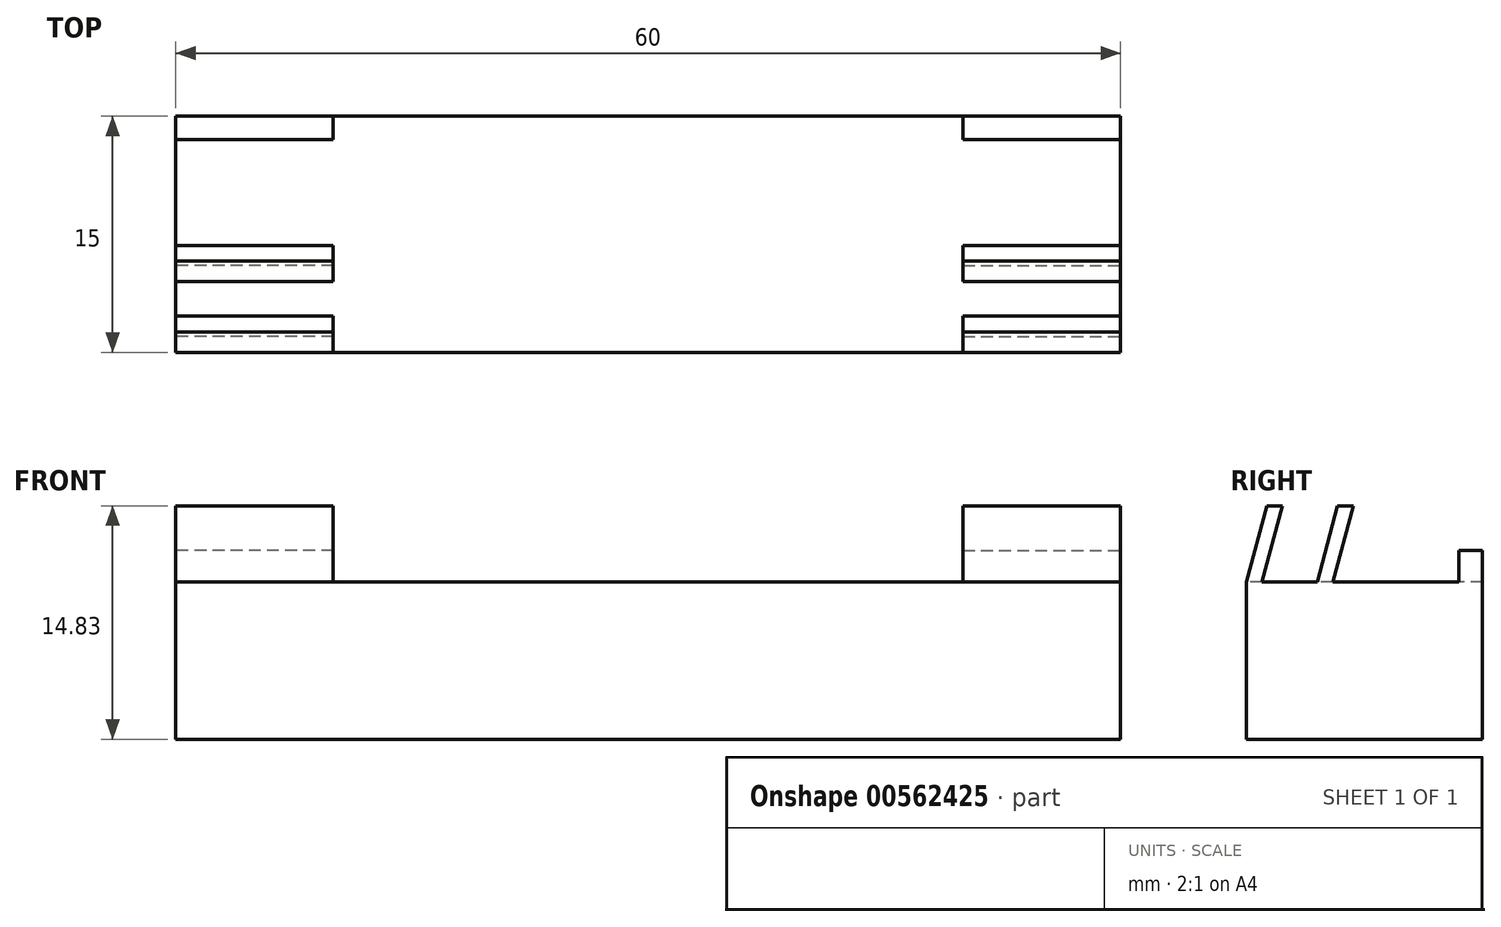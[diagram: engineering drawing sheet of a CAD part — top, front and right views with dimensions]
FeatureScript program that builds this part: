
annotation { "Feature Type Name" : "Feature", "Feature Type Description" : "" }
export const myFeature = defineFeature(function(context is Context, id is Id, definition is map)
    precondition{}
    {
        {
            var Q0;
            Q0=qCreatedBy(makeId("Top.planeOp"),FACE);
            var sketch = newSketch(context, id + "F0", { "sketchPlane" : qUnion([Q0])});
            skLineSegment(sketch, "E0.bottom", {"start": v(-30, 7.5) * mm, "end": v(30, 7.5) * mm});
            skLineSegment(sketch, "E0.top", {"start": v(-30, -7.5) * mm, "end": v(30, -7.5) * mm});
            skLineSegment(sketch, "E0.left", {"start": v(-30, 7.5) * mm, "end": v(-30, -7.5) * mm});
            skLineSegment(sketch, "E0.right", {"start": v(30, 7.5) * mm, "end": v(30, -7.5) * mm});
            skPoint(sketch, "E0.middle", {"position": v(0, 0) * mm});
            skSolve(sketch);
        }
        {
            var Q0;
            Q0=makeQuery(id+"F0.imprint","IMPRINT",FACE,{"disambiguationData":[TD([[makeQuery(id+"F0.imprint","IMPRINT",EDGE,{"derivedFrom":sQuery(id+"F0.wireOp",EDGE,"E0.bottom")}),-1.0]])]});
            extrude(context, id + "F1", {"entities" : qUnion([Q0]), "depth" : 10 * mm, "offsetDistance" : 25 * mm});
        }
        {
            var Q0;
            Q0=makeQuery(id+"F1.opExtrude","SWEPT_FACE",FACE,{"disambiguationData":[OSD([sQuery(id+"F0.wireOp",EDGE,"E0.right")])]});
            var sketch = newSketch(context, id + "F2", { "sketchPlane" : qUnion([Q0])});
            skLineSegment(sketch, "E1.0", {"start": v(7.5, 10) * mm, "end": v(-7.5, 10) * mm});
            skLineSegment(sketch, "E2", {"start": v(-7.5, 10) * mm, "end": v(-6.2, 14.83) * mm});
            skLineSegment(sketch, "E3.0", {"start": v(-7.5, 10) * mm, "end": v(-7.5, 0) * mm, "construction": true});
            skLineSegment(sketch, "E4.1.0.0", {"start": v(-6.5, 10) * mm, "end": v(-5.2, 14.83) * mm});
            skLineSegment(sketch, "E4.direction1", {"start": v(-7.5, 10) * mm, "end": v(-6.5, 10) * mm, "construction": true});
            skLineSegment(sketch, "E5", {"start": v(-6.2, 14.83) * mm, "end": v(-5.2, 14.83) * mm});
            skLineSegment(sketch, "E6.1.0.0", {"start": v(-3, 10) * mm, "end": v(-1.7, 14.83) * mm});
            skLineSegment(sketch, "E6.1.0.1", {"start": v(-2, 10) * mm, "end": v(-0.7, 14.83) * mm});
            skLineSegment(sketch, "E6.1.0.2", {"start": v(-1.7, 14.83) * mm, "end": v(-0.7, 14.83) * mm});
            skLineSegment(sketch, "E6.1.0.3", {"start": v(-3, 10) * mm, "end": v(-2, 10) * mm, "construction": true});
            skLineSegment(sketch, "E6.direction1", {"start": v(-7.5, 10) * mm, "end": v(-3, 10) * mm, "construction": true});
            skLineSegment(sketch, "E7", {"start": v(-2, 10) * mm, "end": v(6, 10) * mm});
            skLineSegment(sketch, "E8", {"start": v(6, 10) * mm, "end": v(6, 12) * mm});
            skLineSegment(sketch, "E9", {"start": v(6, 12) * mm, "end": v(7.5, 12) * mm});
            skLineSegment(sketch, "E10", {"start": v(7.5, 12) * mm, "end": v(7.5, 10) * mm});
            skSolve(sketch);
        }
        {
            var Q0;
            {var subQ0=sQuery(id+"F2.wireOp",EDGE,"E2");Q0=makeQuery(id+"F2.imprint","IMPRINT",FACE,{"disambiguationData":[TD([[makeQuery(id+"F2.imprint","IMPRINT",EDGE,{"derivedFrom":subQ0}),-1.0]])]});}
            var Q1;
            {var subQ0=sQuery(id+"F2.wireOp",EDGE,"E6.1.0.0");Q1=makeQuery(id+"F2.imprint","IMPRINT",FACE,{"disambiguationData":[TD([[makeQuery(id+"F2.imprint","IMPRINT",EDGE,{"derivedFrom":subQ0}),-1.0]])]});}
            var Q2;
            {var subQ2=sQuery(id+"F2.wireOp",EDGE,"E8");Q2=makeQuery(id+"F2.imprint","IMPRINT",FACE,{"disambiguationData":[TD([[makeQuery(id+"F2.imprint","IMPRINT",EDGE,{"derivedFrom":subQ2}),-1.0]])]});}
            var Q3;
            Q3=makeQuery(id+"F1.opExtrude","SWEPT_FACE",FACE,{"disambiguationData":[OSD([sQuery(id+"F0.wireOp",EDGE,"E0.left")])]});
            extrude(context, id + "F3", {"entities" : qUnion([Q0, Q1, Q2]), "operationType" : NewBodyOperationType.ADD, "oppositeDirection" : true, "depth" : 10 * mm, "endBoundEntityFace" : qUnion([Q3]), "offsetDistance" : 25 * mm});
        }
        {
            var Q0;
            Q0=makeQuery(id+"F1.opExtrude","SWEPT_BODY",BODY,{"disambiguationData":[OSD([sQuery(id+"F0.wireOp",EDGE,"E0.bottom"),sQuery(id+"F0.wireOp",EDGE,"E0.top"),sQuery(id+"F0.wireOp",EDGE,"E0.left"),sQuery(id+"F0.wireOp",EDGE,"E0.right")])]});
            var Q1;
            Q1=qCreatedBy(makeId("Right.planeOp"),FACE);
            mirror(context, id + "F4", {"operationType" : NewBodyOperationType.ADD, "entities" : qUnion([Q0]), "mirrorPlane" : qUnion([Q1])});
        }
    });
